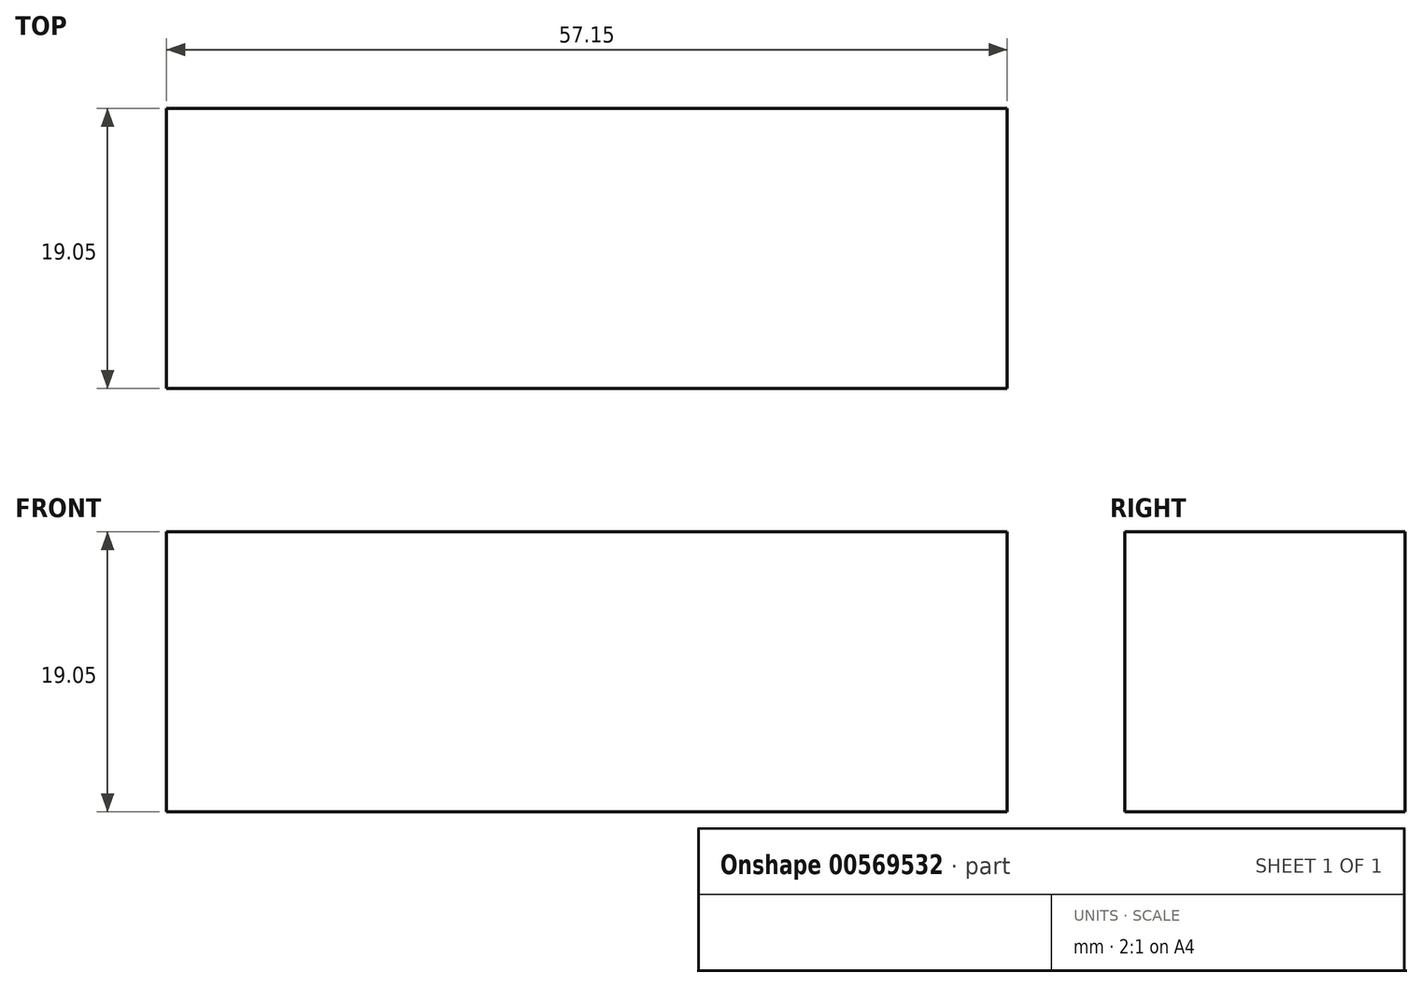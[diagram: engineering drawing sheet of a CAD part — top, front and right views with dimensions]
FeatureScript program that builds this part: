
annotation { "Feature Type Name" : "Feature", "Feature Type Description" : "" }
export const myFeature = defineFeature(function(context is Context, id is Id, definition is map)
    precondition{}
    {
        {
            var Q0;
            Q0=qCreatedBy(makeId("Front.planeOp"),FACE);
            var sketch = newSketch(context, id + "F0", { "sketchPlane" : qUnion([Q0])});
            skLineSegment(sketch, "E0.bottom", {"start": v(0, 0) * mm, "end": v(57.15, 0) * mm});
            skLineSegment(sketch, "E0.top", {"start": v(0, 19.05) * mm, "end": v(57.15, 19.05) * mm});
            skLineSegment(sketch, "E0.left", {"start": v(0, 0) * mm, "end": v(0, 19.05) * mm});
            skLineSegment(sketch, "E0.right", {"start": v(57.15, 0) * mm, "end": v(57.15, 19.05) * mm});
            skSolve(sketch);
        }
        {
            var Q0;
            Q0=makeQuery(id+"F0.imprint","IMPRINT",FACE,{"disambiguationData":[TD([[makeQuery(id+"F0.imprint","IMPRINT",EDGE,{"derivedFrom":sQuery(id+"F0.wireOp",EDGE,"E0.bottom")}),1.0]])]});
            extrude(context, id + "F1", {"entities" : qUnion([Q0]), "depth" : 19.05 * mm, "offsetDistance" : 25.4 * mm});
        }
    });
